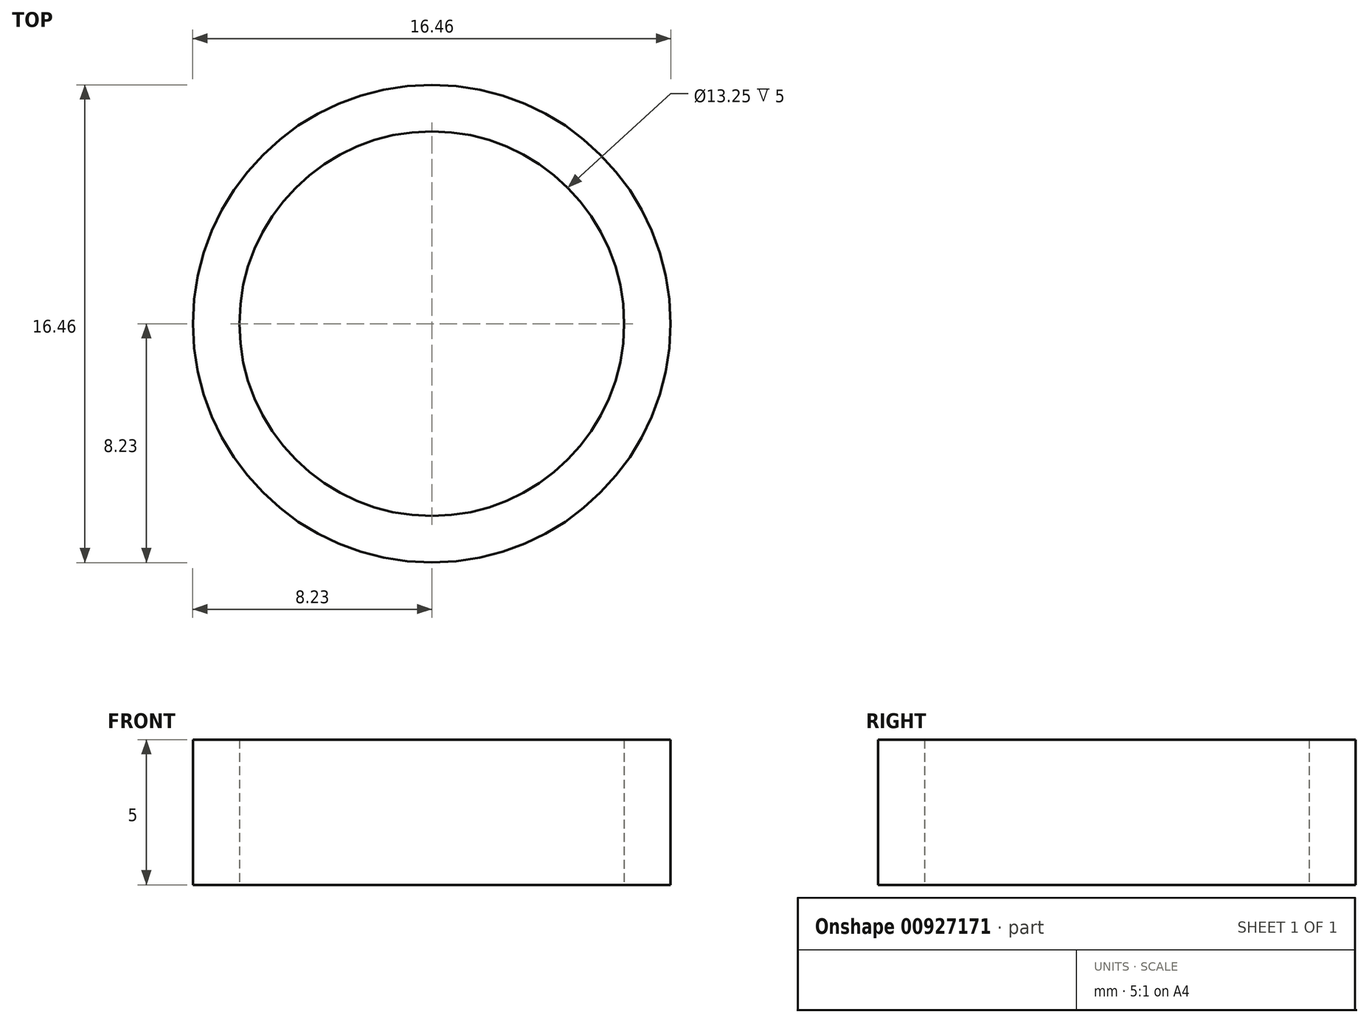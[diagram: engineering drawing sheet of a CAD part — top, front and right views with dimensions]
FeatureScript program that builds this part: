
annotation { "Feature Type Name" : "Feature", "Feature Type Description" : "" }
export const myFeature = defineFeature(function(context is Context, id is Id, definition is map)
    precondition{}
    {
        {
            var Q0;
            Q0=qCreatedBy(makeId("Top.planeOp"),FACE);
            var sketch = newSketch(context, id + "F0", { "sketchPlane" : qUnion([Q0])});
            skCircle(sketch, "E0", {"center": v(0, 0) * mm, "radius": 8.22 * mm});
            skCircle(sketch, "E1", {"center": v(0, 0) * mm, "radius": 6.62 * mm});
            skSolve(sketch);
        }
        {
            var Q0;
            Q0=makeQuery(id+"F0.imprint","IMPRINT",FACE,{"disambiguationData":[TD([[makeQuery(id+"F0.imprint","IMPRINT",EDGE,{"derivedFrom":sQuery(id+"F0.wireOp",EDGE,"E0")}),1.0]])]});
            extrude(context, id + "F1", {"entities" : qUnion([Q0]), "depth" : 5 * mm, "offsetDistance" : 25 * mm});
        }
    });
